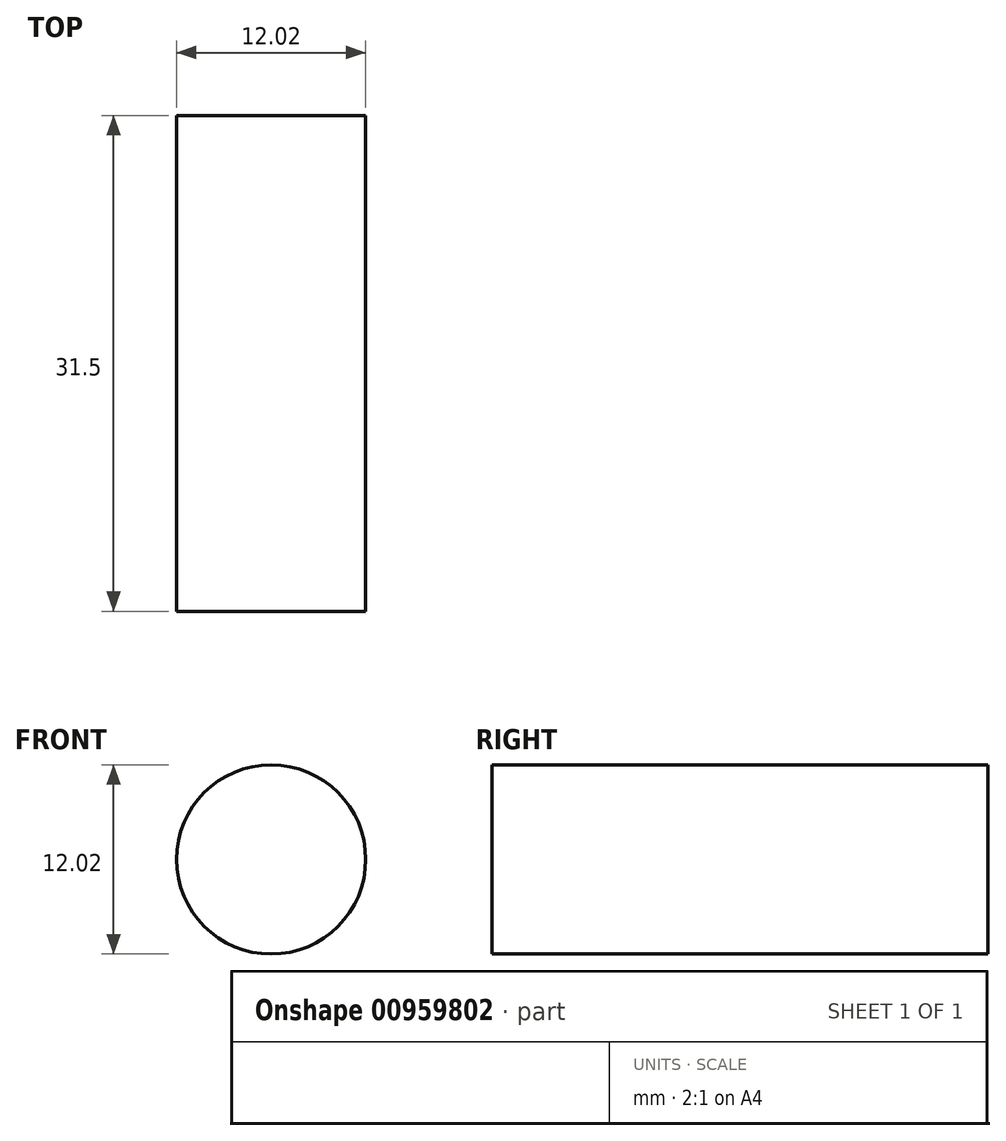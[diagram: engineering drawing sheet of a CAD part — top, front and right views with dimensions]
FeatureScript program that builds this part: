
annotation { "Feature Type Name" : "Feature", "Feature Type Description" : "" }
export const myFeature = defineFeature(function(context is Context, id is Id, definition is map)
    precondition{}
    {
        {
            var Q0;
            Q0=qCreatedBy(makeId("Front.planeOp"),FACE);
            var sketch = newSketch(context, id + "F0", { "sketchPlane" : qUnion([Q0])});
            skCircle(sketch, "E0", {"center": v(0, 0) * mm, "radius": 6 * mm});
            skSolve(sketch);
        }
        {
            var Q0;
            Q0=makeQuery(id+"F0.imprint","IMPRINT",FACE,{"disambiguationData":[TD([[makeQuery(id+"F0.imprint","IMPRINT",EDGE,{"derivedFrom":sQuery(id+"F0.wireOp",EDGE,"E0")}),1.0]])]});
            extrude(context, id + "F1", {"entities" : qUnion([Q0]), "depth" : 31.5 * mm, "offsetDistance" : 25.4 * mm});
        }
    });
